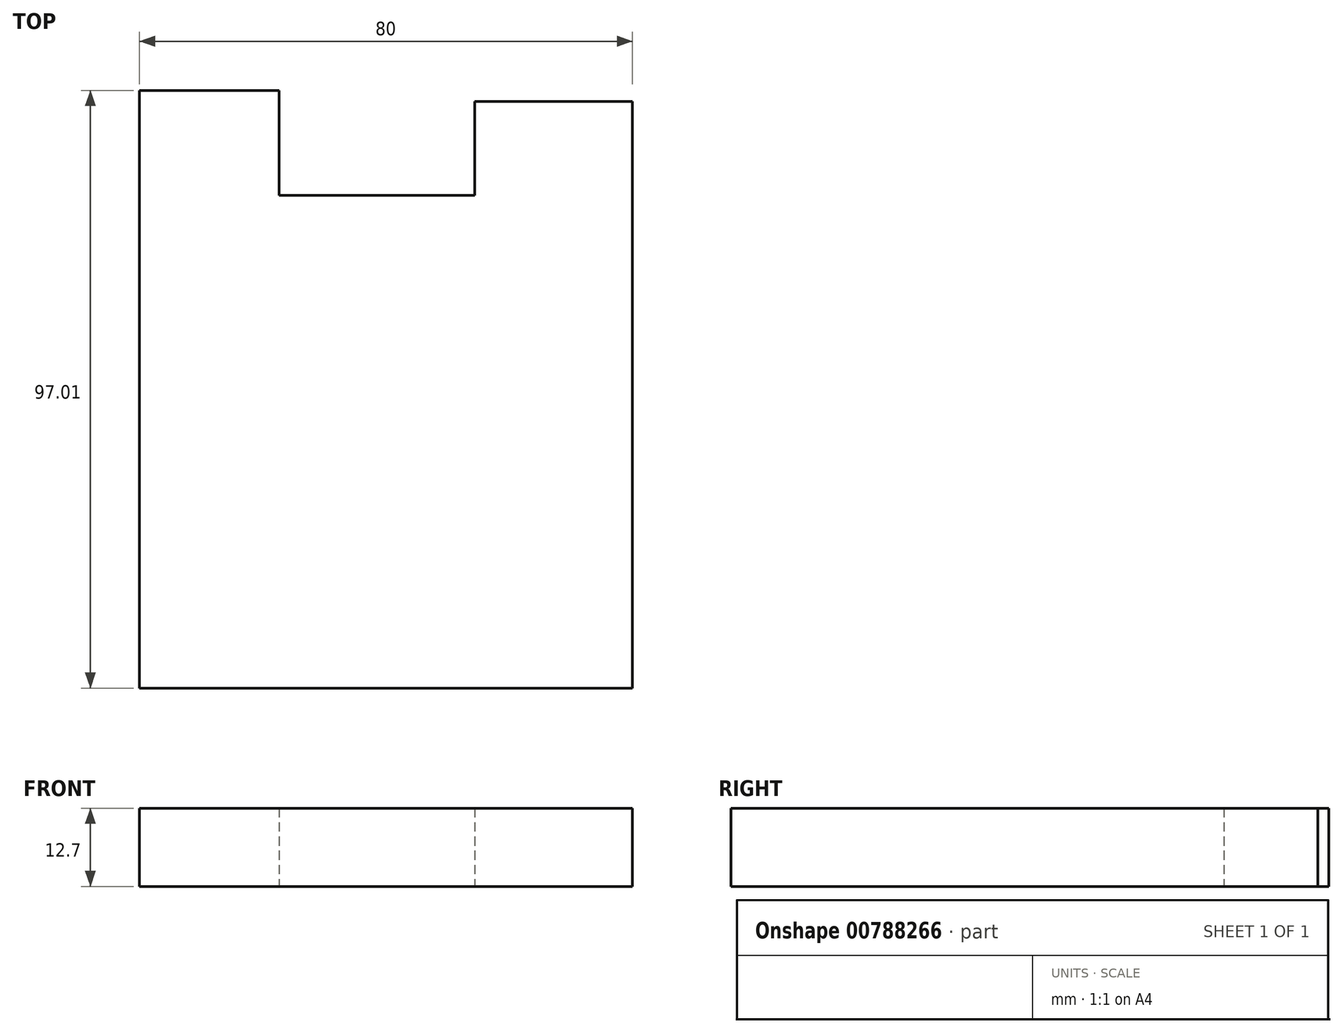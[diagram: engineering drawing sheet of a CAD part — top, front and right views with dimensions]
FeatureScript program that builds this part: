
annotation { "Feature Type Name" : "Feature", "Feature Type Description" : "" }
export const myFeature = defineFeature(function(context is Context, id is Id, definition is map)
    precondition{}
    {
        {
            var Q0;
            Q0=qCreatedBy(makeId("Top.planeOp"),FACE);
            var sketch = newSketch(context, id + "F0", { "sketchPlane" : qUnion([Q0])});
            skLineSegment(sketch, "E0.top", {"start": v(-54.4, -79.04) * mm, "end": v(25.6, -79.04) * mm});
            skLineSegment(sketch, "E0.left", {"start": v(-54.4, 0.96) * mm, "end": v(-54.4, -79.04) * mm});
            skLineSegment(sketch, "E0.right", {"start": v(25.6, 0.96) * mm, "end": v(25.6, -79.04) * mm});
            skLineSegment(sketch, "E1.top", {"start": v(-54.4, 17.97) * mm, "end": v(-31.78, 17.97) * mm});
            skLineSegment(sketch, "E1.left", {"start": v(-54.4, 0.96) * mm, "end": v(-54.4, 17.97) * mm});
            skLineSegment(sketch, "E1.right", {"start": v(-31.78, 0.96) * mm, "end": v(-31.78, 17.97) * mm});
            skLineSegment(sketch, "E2.top", {"start": v(25.6, 16.18) * mm, "end": v(0, 16.18) * mm});
            skLineSegment(sketch, "E2.left", {"start": v(25.6, 0.96) * mm, "end": v(25.6, 16.18) * mm});
            skLineSegment(sketch, "E2.right", {"start": v(0, 0.96) * mm, "end": v(0, 16.18) * mm});
            skLineSegment(sketch, "E3", {"start": v(-31.78, 0.96) * mm, "end": v(0, 0.96) * mm});
            skSolve(sketch);
        }
        {
            var Q0;
            Q0 = qSketchRegion(id + "F0", true);
            extrude(context, id + "F1", {"entities" : qUnion([Q0]), "depth" : 12.7 * mm, "offsetDistance" : 25.4 * mm});
        }
    });
